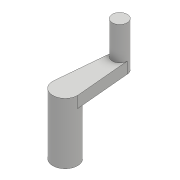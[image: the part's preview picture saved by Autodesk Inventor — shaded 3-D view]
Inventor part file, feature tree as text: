
AUTODESK INVENTOR PART (.ipt)
format: ipt  version: 2017 (Build 210142000, 142)  size: 92,160 bytes
history: native  units: mm
features: extrude x3, sketch x2
ambient origin geometry x8: Origin, YZ Plane, XZ Plane, XY Plane, X Axis, Y Axis, Z Axis, Center Point
bodies: Solid1 (feature_tree)
feature tree (5):
  extrude  "Extrusion1"  Depth=50.0mm TaperAngle=0.0deg
  sketch  "Sketch2"  dims[d3=15.0mm d4=11.5mm d5=0.0mm d6=45.0mm d7=0.0mm]
  extrude  "Extrusion2"  Depth=11.5mm TaperAngle=0.0deg
  extrude  "Extrusion3"  Depth=45.0mm TaperAngle=0.0deg
  sketch  "Sketch1"  dims[d0=25.0mm d1=50.0mm d2=0.0mm]
